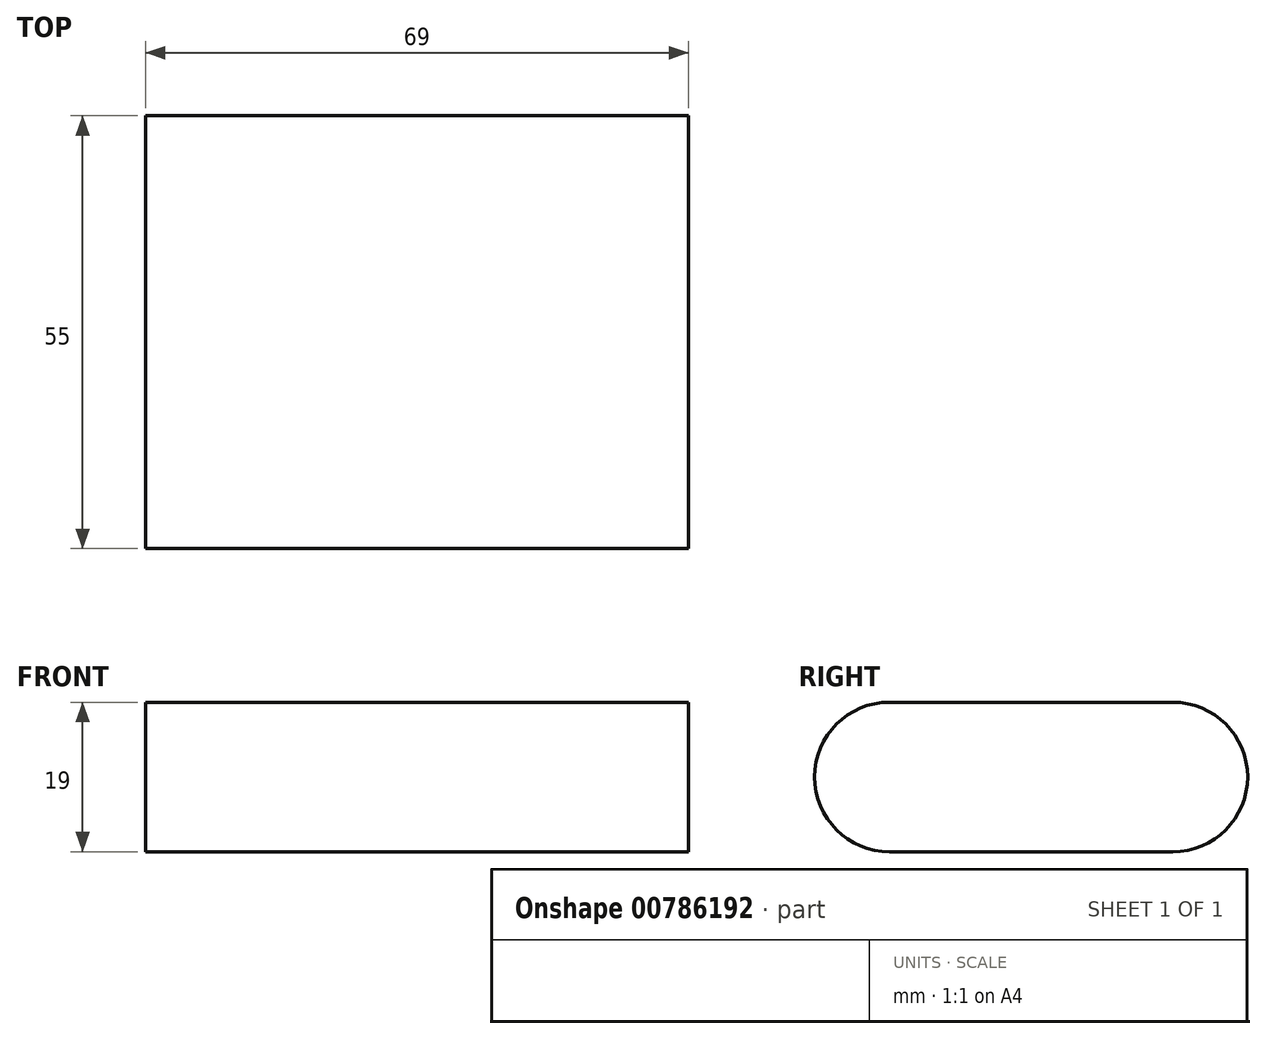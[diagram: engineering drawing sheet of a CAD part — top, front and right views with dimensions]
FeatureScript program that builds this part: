
annotation { "Feature Type Name" : "Feature", "Feature Type Description" : "" }
export const myFeature = defineFeature(function(context is Context, id is Id, definition is map)
    precondition{}
    {
        {
            assignVariable(context, id + "F0", {"name" : "height", "anyValue" : 19 * mm});
        }
        {
            var Q0;
            Q0=qCreatedBy(makeId("Top.planeOp"),FACE);
            var sketch = newSketch(context, id + "F1", { "sketchPlane" : qUnion([Q0])});
            skLineSegment(sketch, "E0.bottom", {"start": v(-32.71, 28.3) * mm, "end": v(36.29, 28.3) * mm});
            skLineSegment(sketch, "E0.top", {"start": v(-32.71, -26.7) * mm, "end": v(36.29, -26.7) * mm});
            skLineSegment(sketch, "E0.left", {"start": v(-32.71, 28.3) * mm, "end": v(-32.71, -26.7) * mm});
            skLineSegment(sketch, "E0.right", {"start": v(36.29, 28.3) * mm, "end": v(36.29, -26.7) * mm});
            skSolve(sketch);
        }
        {
            var Q0;
            Q0=makeQuery(id+"F1.imprint","IMPRINT",FACE,{"disambiguationData":[TD([[makeQuery(id+"F1.imprint","IMPRINT",EDGE,{"derivedFrom":sQuery(id+"F1.wireOp",EDGE,"E0.bottom")}),-1.0]])]});
            extrude(context, id + "F2", {"entities" : qUnion([Q0]), "depth" : getVariable(context, 'height'), "offsetDistance" : 25 * mm});
        }
        {
            var Q0;
            Q0=makeQuery(id+"F2.opExtrude","CAP_EDGE",EDGE,{"disambiguationData":[OSD([sQuery(id+"F1.wireOp",EDGE,"E0.top")])],"isStart":false});
            var Q1;
            Q1=makeQuery(id+"F2.opExtrude","CAP_EDGE",EDGE,{"disambiguationData":[OSD([sQuery(id+"F1.wireOp",EDGE,"E0.top")])],"isStart":true});
            var Q2;
            Q2=makeQuery(id+"F2.opExtrude","CAP_EDGE",EDGE,{"disambiguationData":[OSD([sQuery(id+"F1.wireOp",EDGE,"E0.bottom")])],"isStart":false});
            var Q3;
            Q3=makeQuery(id+"F2.opExtrude","CAP_EDGE",EDGE,{"disambiguationData":[OSD([sQuery(id+"F1.wireOp",EDGE,"E0.bottom")])],"isStart":true});
            fillet(context, id + "F3", {"entities" : qUnion([Q0, Q1, Q2, Q3]), "radius" : getVariable(context, 'height') / 2, "tangentPropagation" : true, "allowEdgeOverflow" : false});
        }
    });
